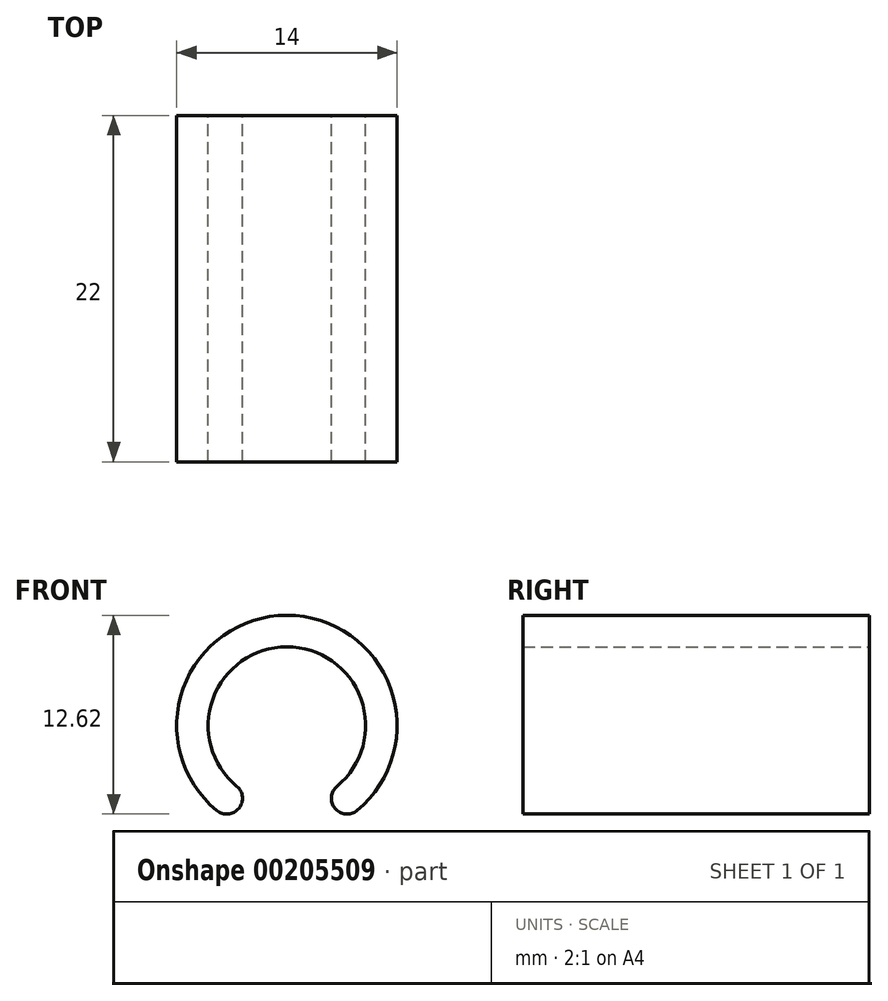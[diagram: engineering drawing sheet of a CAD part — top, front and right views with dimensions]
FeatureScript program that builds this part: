
annotation { "Feature Type Name" : "Feature", "Feature Type Description" : "" }
export const myFeature = defineFeature(function(context is Context, id is Id, definition is map)
    precondition{}
    {
        {
            var Q0;
            Q0=qCreatedBy(makeId("Front.planeOp"),FACE);
            var sketch = newSketch(context, id + "F0", { "sketchPlane" : qUnion([Q0])});
            skCircle(sketch, "E0", {"center": v(0, 0) * mm, "radius": 4 * mm});
            skCircle(sketch, "E1.0", {"center": v(0, 0) * mm, "radius": 5 * mm});
            skCircle(sketch, "E2.0", {"center": v(0, 0) * mm, "radius": 7 * mm});
            skLineSegment(sketch, "E3", {"start": v(0, 0) * mm, "end": v(6.4, -11.08) * mm});
            skLineSegment(sketch, "E4", {"start": v(0, 0) * mm, "end": v(-6.8, -11.78) * mm});
            skPoint(sketch, "E5", {"position": v(2, -3.46) * mm});
            skPoint(sketch, "E6", {"position": v(-2, -3.46) * mm});
            skSolve(sketch);
        }
        {
            var Q0;
            {var subQ0=sQuery(id+"F0.wireOp",EDGE,"E3");var subQ1=sQuery(id+"F0.wireOp",EDGE,"E1.0");var subQ2=makeQuery(id+"F0.imprint","INTERSECT",VERTEX,{"derivedFrom":[subQ1,subQ0]});Q0=makeQuery(id+"F0.imprint","IMPRINT",FACE,{"disambiguationData":[TD([[makeQuery(id+"F0.imprint","IMPRINT",EDGE,{"disambiguationData":[TD([[subQ2,-1.0]])],"derivedFrom":subQ1}),-1.0]])]});}
            extrude(context, id + "F1", {"entities" : qUnion([Q0]), "endBound" : BoundingType.SYMMETRIC, "depth" : 22 * mm});
        }
        {
            var Q0;
            Q0=makeQuery(id+"F1.opExtrude","SWEPT_EDGE",EDGE,{"disambiguationData":[OSD([sQuery(id+"F0.wireOp",EDGE,"E2.0"),sQuery(id+"F0.wireOp",EDGE,"E3")])]});
            var Q1;
            Q1=makeQuery(id+"F1.opExtrude","SWEPT_EDGE",EDGE,{"disambiguationData":[OSD([sQuery(id+"F0.wireOp",EDGE,"E0"),sQuery(id+"F0.wireOp",EDGE,"E3")])]});
            var Q2;
            Q2=makeQuery(id+"F1.opExtrude","SWEPT_EDGE",EDGE,{"disambiguationData":[OSD([sQuery(id+"F0.wireOp",EDGE,"E0"),sQuery(id+"F0.wireOp",EDGE,"E4")])]});
            var Q3;
            Q3=makeQuery(id+"F1.opExtrude","SWEPT_EDGE",EDGE,{"disambiguationData":[OSD([sQuery(id+"F0.wireOp",EDGE,"E2.0"),sQuery(id+"F0.wireOp",EDGE,"E4")])]});
            fillet(context, id + "F2", {"entities" : qUnion([Q0, Q1, Q2, Q3]), "radius" : 1 * mm, "tangentPropagation" : true, "allowEdgeOverflow" : false});
        }
    });
